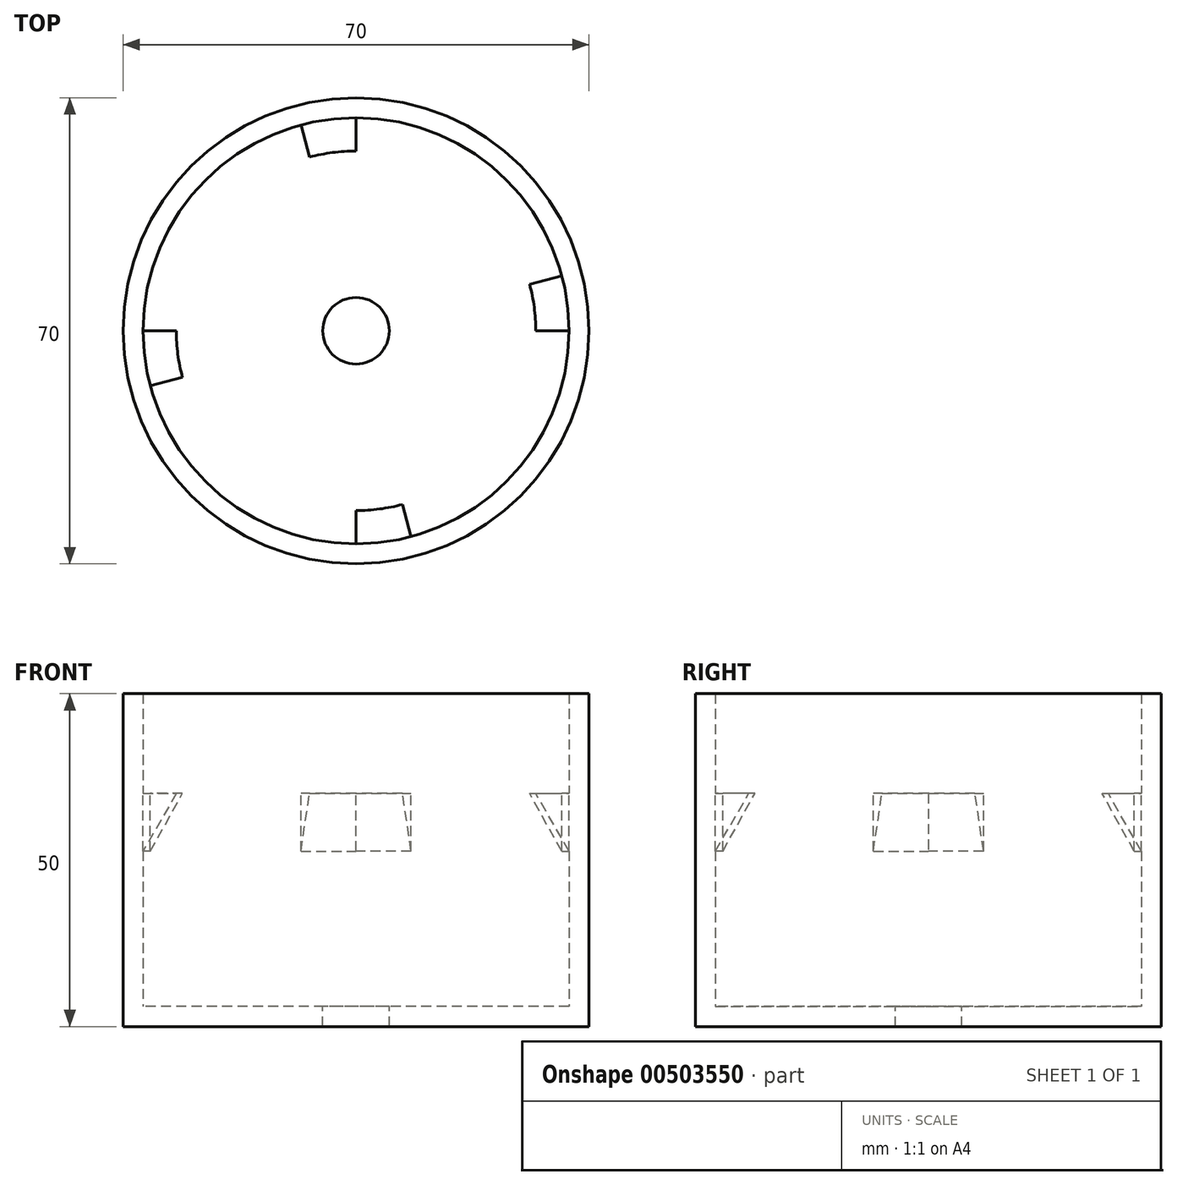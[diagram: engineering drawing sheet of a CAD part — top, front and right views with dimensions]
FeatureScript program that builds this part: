
annotation { "Feature Type Name" : "Feature", "Feature Type Description" : "" }
export const myFeature = defineFeature(function(context is Context, id is Id, definition is map)
    precondition{}
    {
        {
            var Q0;
            Q0=qCreatedBy(makeId("Top.planeOp"),FACE);
            var sketch = newSketch(context, id + "F0", { "sketchPlane" : qUnion([Q0])});
            skCircle(sketch, "E0", {"center": v(0, 0) * mm, "radius": 35 * mm});
            skSolve(sketch);
        }
        {
            var Q0;
            Q0 = qSketchRegion(id + "F0", true);
            extrude(context, id + "F1", {"entities" : qUnion([Q0]), "depth" : 50 * mm});
        }
        {
            var Q0;
            Q0=makeQuery(id+"F1.opExtrude","CAP_FACE",FACE,{"disambiguationData":[OSD([sQuery(id+"F0.wireOp",EDGE,"E0")])],"isStart":false});
            shell(context, id + "F2", {"entities" : qUnion([Q0]), "thickness" : 3 * mm});
        }
        {
            var Q0;
            Q0=qCreatedBy(makeId("Right.planeOp"),FACE);
            var sketch = newSketch(context, id + "F3", { "sketchPlane" : qUnion([Q0])});
            skLineSegment(sketch, "E1", {"start": v(-32, 35) * mm, "end": v(-27, 35) * mm});
            skLineSegment(sketch, "E2", {"start": v(-32, 3) * mm, "end": v(-32, 100) * mm, "construction": true});
            skLineSegment(sketch, "E3", {"start": v(32, 100) * mm, "end": v(32, 3) * mm, "construction": true});
            skLineSegment(sketch, "E4", {"start": v(-27, 35) * mm, "end": v(-32, 26.34) * mm});
            skLineSegment(sketch, "E5", {"start": v(-32, 35) * mm, "end": v(-32, 26.34) * mm});
            skLineSegment(sketch, "E6", {"start": v(0, 0) * mm, "end": v(0, 100.65) * mm, "construction": true});
            skSolve(sketch);
        }
        {
            var Q0;
            Q0 = qSketchRegion(id + "F3", true);
            var Q1;
            Q1=sQuery(id+"F3.wireOp",EDGE,"E6");
            revolve(context, id + "F4", {"operationType" : NewBodyOperationType.ADD, "entities" : qUnion([Q0]), "axis" : qUnion([Q1]), "revolveType" : RevolveType.FULL});
        }
        {
            var Q0;
            Q0=makeQuery(id+"F4.opRevolve","SWEPT_FACE",FACE,{"disambiguationData":[OSD([sQuery(id+"F3.wireOp",EDGE,"E1")])]});
            var sketch = newSketch(context, id + "F5", { "sketchPlane" : qUnion([Q0])});
            skLineSegment(sketch, "E7", {"start": v(-32, 0) * mm, "end": v(0, 0) * mm});
            skLineSegment(sketch, "E8", {"start": v(0, 0) * mm, "end": v(-30.9, -8.28) * mm});
            skLineSegment(sketch, "E9", {"start": v(0, 0) * mm, "end": v(0, -32) * mm});
            skLineSegment(sketch, "E10", {"start": v(0, 0) * mm, "end": v(8.28, -30.9) * mm});
            skLineSegment(sketch, "E11", {"start": v(0, 0) * mm, "end": v(32, 0) * mm});
            skLineSegment(sketch, "E12", {"start": v(0, 0) * mm, "end": v(30.9, 8.28) * mm});
            skLineSegment(sketch, "E13", {"start": v(0, 0) * mm, "end": v(0, 32) * mm});
            skLineSegment(sketch, "E14", {"start": v(0, 0) * mm, "end": v(-8.28, 30.9) * mm});
            skArc(sketch, "E15", {"start": v(-32, 0) * mm, "mid": v(-25.39, 19.48) * mm, "end": v(-8.28, 30.9) * mm});
            skArc(sketch, "E16", {"start": v(0, 32) * mm, "mid": v(19.48, 25.39) * mm, "end": v(30.9, 8.28) * mm});
            skArc(sketch, "E17", {"start": v(32, 0) * mm, "mid": v(25.39, -19.48) * mm, "end": v(8.28, -30.9) * mm});
            skArc(sketch, "E18", {"start": v(0, -32) * mm, "mid": v(-19.48, -25.39) * mm, "end": v(-30.9, -8.28) * mm});
            skSolve(sketch);
        }
        {
            var Q0;
            Q0 = qSketchRegion(id + "F5", true);
            extrude(context, id + "F6", {"entities" : qUnion([Q0]), "operationType" : NewBodyOperationType.REMOVE, "oppositeDirection" : true, "depth" : 25 * mm});
        }
        {
            var Q0;
            {var subQ0=sQuery(id+"F0.wireOp",EDGE,"E0");Q0=makeQuery(id+"F2.opShell","OFFSET_FACE",FACE,{"disambiguationData":[OSD([subQ0]),TDD([makeQuery(id+"F1.opExtrude","CAP_FACE",FACE,{"disambiguationData":[OSD([subQ0])],"isStart":true})])]});}
            var sketch = newSketch(context, id + "F7", { "sketchPlane" : qUnion([Q0])});
            skCircle(sketch, "E19", {"center": v(0, 0) * mm, "radius": 5 * mm});
            skSolve(sketch);
        }
        {
            var Q0;
            Q0 = qSketchRegion(id + "F7", true);
            extrude(context, id + "F8", {"entities" : qUnion([Q0]), "operationType" : NewBodyOperationType.REMOVE, "oppositeDirection" : true, "depth" : 25 * mm});
        }
    });
